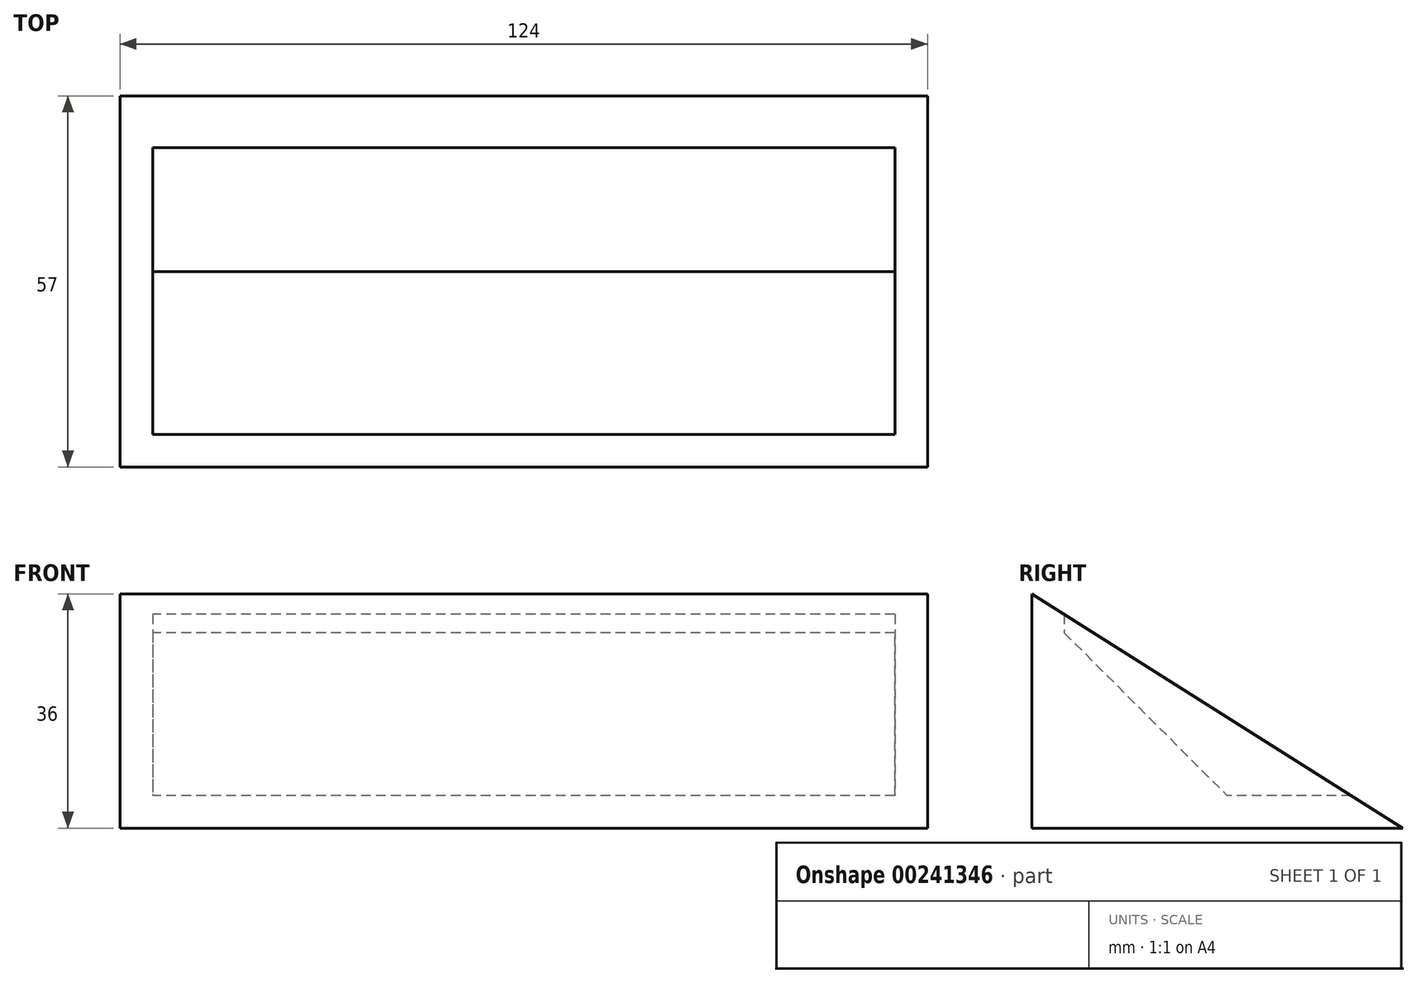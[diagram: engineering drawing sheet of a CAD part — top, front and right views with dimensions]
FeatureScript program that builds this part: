
annotation { "Feature Type Name" : "Feature", "Feature Type Description" : "" }
export const myFeature = defineFeature(function(context is Context, id is Id, definition is map)
    precondition{}
    {
        {
            var Q0;
            Q0=qCreatedBy(makeId("Right.planeOp"),FACE);
            var sketch = newSketch(context, id + "F0", { "sketchPlane" : qUnion([Q0])});
            skLineSegment(sketch, "E0", {"start": v(-20, 0) * mm, "end": v(-20, 36) * mm});
            skLineSegment(sketch, "E1", {"start": v(-20, 36) * mm, "end": v(37, 0) * mm});
            skLineSegment(sketch, "E2", {"start": v(37, 0) * mm, "end": v(-20, 0) * mm});
            skSolve(sketch);
        }
        {
            var Q0;
            Q0 = qSketchRegion(id + "F0", true);
            extrude(context, id + "F1", {"entities" : qUnion([Q0]), "depth" : 124 * mm});
        }
        {
            var Q0;
            Q0=makeQuery(id+"F1.opExtrude","SWEPT_FACE",FACE,{"disambiguationData":[OSD([sQuery(id+"F0.wireOp",EDGE,"E2")])]});
            var sketch = newSketch(context, id + "F2", { "sketchPlane" : qUnion([Q0])});
            skLineSegment(sketch, "E3.bottom", {"start": v(5, -37) * mm, "end": v(119, -37) * mm});
            skLineSegment(sketch, "E3.top", {"start": v(5, 15) * mm, "end": v(119, 15) * mm});
            skLineSegment(sketch, "E3.left", {"start": v(5, -37) * mm, "end": v(5, 15) * mm});
            skLineSegment(sketch, "E3.right", {"start": v(119, -37) * mm, "end": v(119, 15) * mm});
            skSolve(sketch);
        }
        {
            var Q0;
            Q0 = qSketchRegion(id + "F2", true);
            extrude(context, id + "F3", {"entities" : qUnion([Q0]), "operationType" : NewBodyOperationType.REMOVE, "endBound" : BoundingType.THROUGH_ALL, "oppositeDirection" : true, "depth" : 25 * mm, "hasSecondDirection" : true, "secondDirectionOppositeDirection" : true, "secondDirectionDepth" : 5 * mm});
        }
        {
            var Q0;
            Q0=makeQuery(id+"F3.boolean.opBoolean","COPY",EDGE,{"derivedFrom":makeQuery(id+"F3.opExtrude","CAP_EDGE",EDGE,{"disambiguationData":[OSD([sQuery(id+"F2.wireOp",EDGE,"E3.top")])],"isStart":true})});
            chamfer(context, id + "F4", {"entities" : qUnion([Q0]), "width" : 25 * mm, "tangentPropagation" : true});
        }
    });
